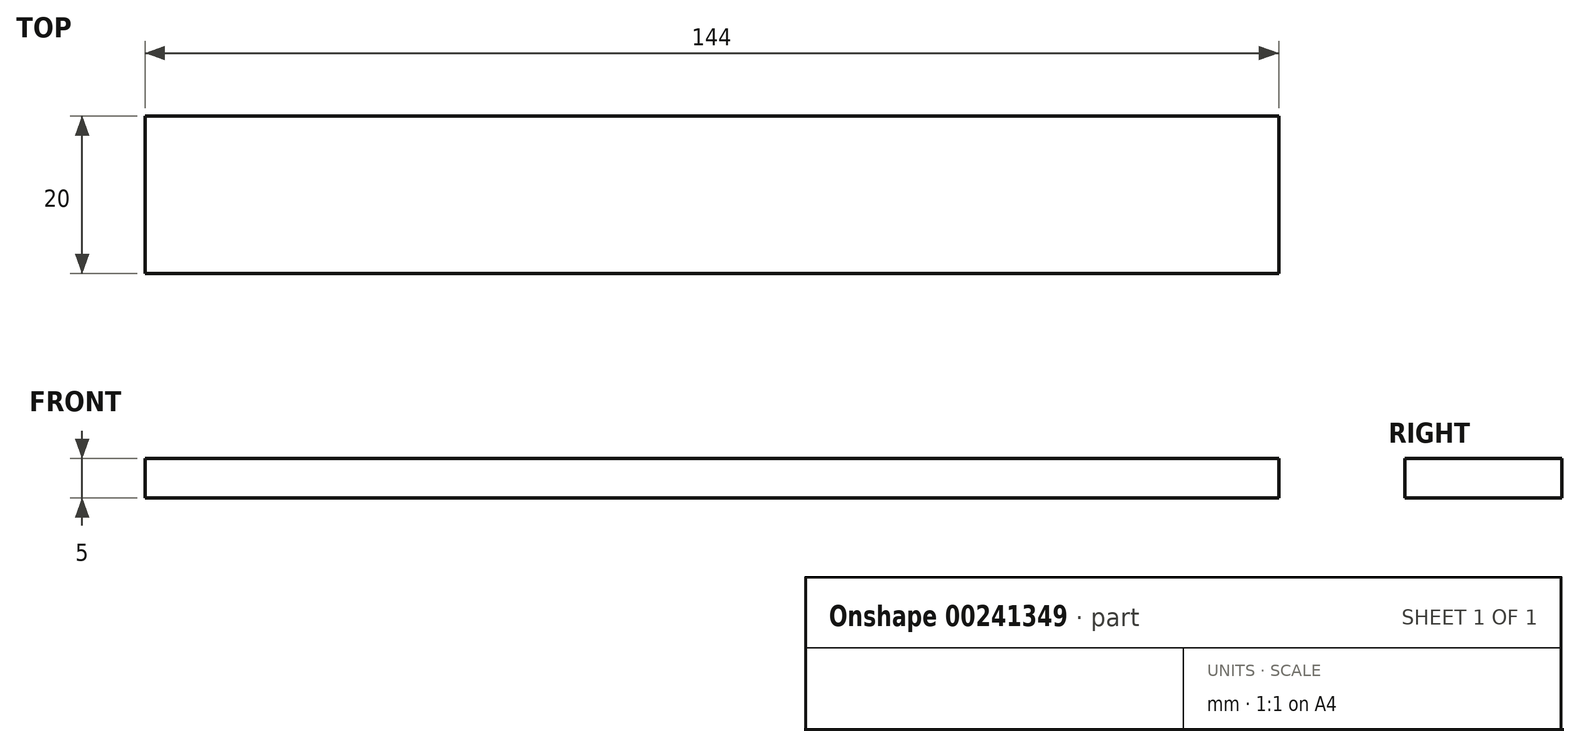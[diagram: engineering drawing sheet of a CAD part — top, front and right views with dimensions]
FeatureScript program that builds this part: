
annotation { "Feature Type Name" : "Feature", "Feature Type Description" : "" }
export const myFeature = defineFeature(function(context is Context, id is Id, definition is map)
    precondition{}
    {
        {
            var Q0;
            Q0=qCreatedBy(makeId("Top.planeOp"),FACE);
            var sketch = newSketch(context, id + "F0", { "sketchPlane" : qUnion([Q0])});
            skLineSegment(sketch, "E0.bottom", {"start": v(-72, 10) * mm, "end": v(72, 10) * mm});
            skLineSegment(sketch, "E0.top", {"start": v(-72, -10) * mm, "end": v(72, -10) * mm});
            skLineSegment(sketch, "E0.left", {"start": v(-72, 10) * mm, "end": v(-72, -10) * mm});
            skLineSegment(sketch, "E0.right", {"start": v(72, 10) * mm, "end": v(72, -10) * mm});
            skPoint(sketch, "E0.middle", {"position": v(0, 0) * mm});
            skSolve(sketch);
        }
        {
            var Q0;
            Q0 = qSketchRegion(id + "F0", true);
            extrude(context, id + "F1", {"entities" : qUnion([Q0]), "depth" : 5 * mm});
        }
    });
